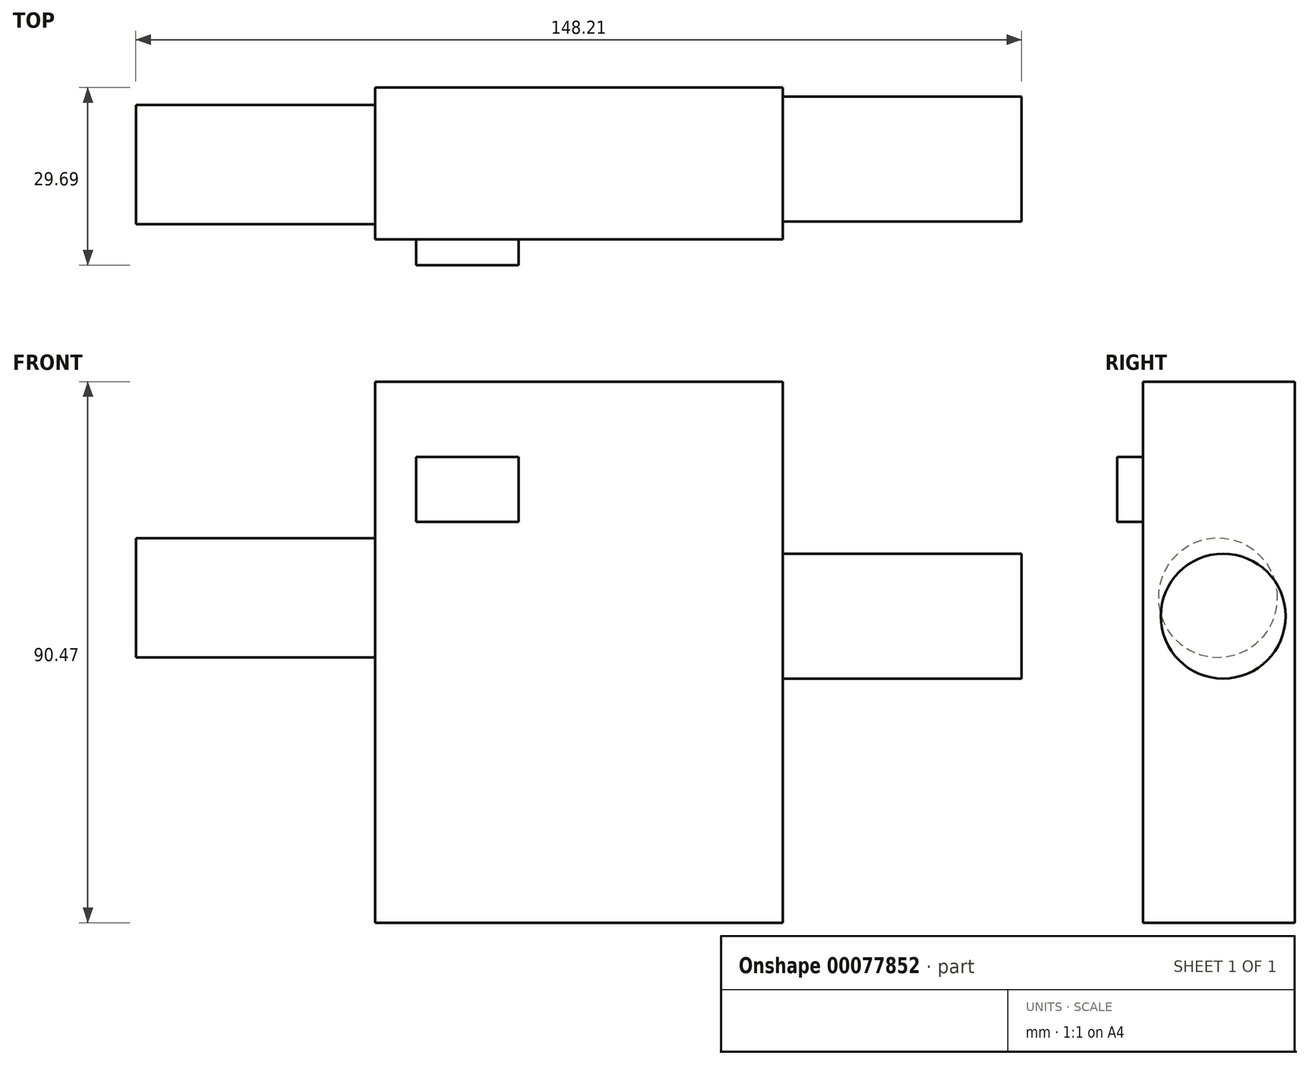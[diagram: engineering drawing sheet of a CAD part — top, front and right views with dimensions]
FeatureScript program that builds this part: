
annotation { "Feature Type Name" : "Feature", "Feature Type Description" : "" }
export const myFeature = defineFeature(function(context is Context, id is Id, definition is map)
    precondition{}
    {
        {
            var Q0;
            Q0=qCreatedBy(makeId("Front.planeOp"),FACE);
            var sketch = newSketch(context, id + "F0", { "sketchPlane" : qUnion([Q0])});
            skLineSegment(sketch, "E0.bottom", {"start": v(-45.36, 44.87) * mm, "end": v(22.85, 44.87) * mm});
            skLineSegment(sketch, "E0.top", {"start": v(-45.36, -45.6) * mm, "end": v(22.85, -45.6) * mm});
            skLineSegment(sketch, "E0.left", {"start": v(-45.36, 44.87) * mm, "end": v(-45.36, -45.6) * mm});
            skLineSegment(sketch, "E0.right", {"start": v(22.85, 44.87) * mm, "end": v(22.85, -45.6) * mm});
            skSolve(sketch);
        }
        {
            var Q0;
            Q0=makeQuery(id+"F0.imprint","IMPRINT",FACE,{"disambiguationData":[TD([[makeQuery(id+"F0.imprint","IMPRINT",EDGE,{"derivedFrom":sQuery(id+"F0.wireOp",EDGE,"E0.bottom")}),-1.0]])]});
            extrude(context, id + "F1", {"entities" : qUnion([Q0]), "depth" : 25.4 * mm});
        }
        {
            var Q0;
            Q0=makeQuery(id+"F1.opExtrude","SWEPT_FACE",FACE,{"disambiguationData":[OSD([sQuery(id+"F0.wireOp",EDGE,"E0.right")])]});
            var sketch = newSketch(context, id + "F2", { "sketchPlane" : qUnion([Q0])});
            skCircle(sketch, "E1", {"center": v(-11.98, 5.67) * mm, "radius": 10.44 * mm});
            skSolve(sketch);
        }
        {
            var Q0;
            Q0=makeQuery(id+"F2.imprint","IMPRINT",FACE,{"disambiguationData":[TD([[makeQuery(id+"F2.imprint","IMPRINT",EDGE,{"derivedFrom":sQuery(id+"F2.wireOp",EDGE,"E1")}),1.0]])]});
            extrude(context, id + "F3", {"entities" : qUnion([Q0]), "operationType" : NewBodyOperationType.ADD, "depth" : 30.08 * mm});
        }
        {
            var Q0;
            Q0=makeQuery(id+"F1.opExtrude","SWEPT_FACE",FACE,{"disambiguationData":[OSD([sQuery(id+"F0.wireOp",EDGE,"E0.left")])]});
            var sketch = newSketch(context, id + "F4", { "sketchPlane" : qUnion([Q0])});
            skCircle(sketch, "E2", {"center": v(12.86, 8.74) * mm, "radius": 9.96 * mm});
            skSolve(sketch);
        }
        {
            var Q0;
            Q0=makeQuery(id+"F4.imprint","IMPRINT",FACE,{"disambiguationData":[TD([[makeQuery(id+"F4.imprint","IMPRINT",EDGE,{"derivedFrom":sQuery(id+"F4.wireOp",EDGE,"E2")}),1.0]])]});
            extrude(context, id + "F5", {"entities" : qUnion([Q0]), "operationType" : NewBodyOperationType.ADD, "depth" : 25.4 * mm});
        }
        {
            var Q0;
            Q0=makeQuery(id+"F5.opExtrude","CAP_FACE",FACE,{"disambiguationData":[OSD([sQuery(id+"F4.wireOp",EDGE,"E2")])],"isStart":false});
            extrude(context, id + "F6", {"entities" : qUnion([Q0]), "operationType" : NewBodyOperationType.ADD, "depth" : 14.65 * mm});
        }
        {
            var Q0;
            Q0=makeQuery(id+"F6.opExtrude","CAP_FACE",FACE,{"disambiguationData":[OSD([sQuery(id+"F4.wireOp",EDGE,"E2")])],"isStart":false});
            extrude(context, id + "F7", {"entities" : qUnion([Q0]), "operationType" : NewBodyOperationType.ADD, "oppositeDirection" : true, "depth" : 77.01 * mm});
        }
        {
            var Q0;
            Q0=makeQuery(id+"F3.opExtrude","CAP_FACE",FACE,{"disambiguationData":[OSD([sQuery(id+"F2.wireOp",EDGE,"E1")])],"isStart":false});
            extrude(context, id + "F8", {"entities" : qUnion([Q0]), "operationType" : NewBodyOperationType.ADD, "depth" : 7.25 * mm});
        }
        {
            var Q0;
            Q0=makeQuery(id+"F8.opExtrude","CAP_FACE",FACE,{"disambiguationData":[OSD([sQuery(id+"F2.wireOp",EDGE,"E1")])],"isStart":false});
            extrude(context, id + "F9", {"entities" : qUnion([Q0]), "operationType" : NewBodyOperationType.ADD, "depth" : 2.6 * mm});
        }
        {
            var Q0;
            Q0=makeQuery(id+"F1.opExtrude","CAP_FACE",FACE,{"disambiguationData":[OSD([sQuery(id+"F0.wireOp",EDGE,"E0.bottom"),sQuery(id+"F0.wireOp",EDGE,"E0.top"),sQuery(id+"F0.wireOp",EDGE,"E0.left"),sQuery(id+"F0.wireOp",EDGE,"E0.right")])],"isStart":false});
            var sketch = newSketch(context, id + "F10", { "sketchPlane" : qUnion([Q0])});
            skLineSegment(sketch, "E3.bottom", {"start": v(-38.48, 32.3) * mm, "end": v(-21.4, 32.3) * mm});
            skLineSegment(sketch, "E3.top", {"start": v(-38.48, 21.45) * mm, "end": v(-21.4, 21.45) * mm});
            skLineSegment(sketch, "E3.left", {"start": v(-38.48, 32.3) * mm, "end": v(-38.48, 21.45) * mm});
            skLineSegment(sketch, "E3.right", {"start": v(-21.4, 32.3) * mm, "end": v(-21.4, 21.45) * mm});
            skSolve(sketch);
        }
        {
            var Q0;
            Q0=makeQuery(id+"F10.imprint","IMPRINT",FACE,{"disambiguationData":[TD([[makeQuery(id+"F10.imprint","IMPRINT",EDGE,{"derivedFrom":sQuery(id+"F10.wireOp",EDGE,"E3.bottom")}),-1.0]])]});
            extrude(context, id + "F11", {"entities" : qUnion([Q0]), "operationType" : NewBodyOperationType.ADD, "depth" : 4.3 * mm});
        }
    });
